annotation { "Feature Type Name" : "Feature", "Feature Type Description" : "" }
export const myFeature = defineFeature(function(context is Context, id is Id, definition is map)
    precondition{}
    {
        {
            assignVariable(context, id + "F0", {"name" : "T", "anyValue" : 0});
        }
        {
            var Q0;
            Q0=qCreatedBy(makeId("Front.planeOp"),FACE);
            var sketch = newSketch(context, id + "F1", { "sketchPlane" : qUnion([Q0])});
            skArc(sketch, "E0", {"start": v(71.88, 0.4) * mm, "mid": v(0, 71.88) * mm, "end": v(-71.88, 0.4) * mm});
            skLineSegment(sketch, "E1", {"start": v(0, 0) * mm, "end": v(35.94, 0) * mm, "construction": true});
            skLineSegment(sketch, "E2.bottom", {"start": v(35.94, 0.4) * mm, "end": v(71.88, 0.4) * mm});
            skLineSegment(sketch, "E2.top", {"start": v(35.94, -0.4) * mm, "end": v(71.88, -0.4) * mm});
            skLineSegment(sketch, "E2.left", {"start": v(35.94, 0.4) * mm, "end": v(35.94, -0.4) * mm});
            skLineSegment(sketch, "E3", {"start": v(0, 0) * mm, "end": v(-35.94, 0) * mm, "construction": true});
            skLineSegment(sketch, "E4.bottom", {"start": v(-0.4, 0) * mm, "end": v(0.4, 0) * mm});
            skLineSegment(sketch, "E4.left", {"start": v(-0.4, 0) * mm, "end": v(-0.4, -71.88) * mm});
            skLineSegment(sketch, "E4.right", {"start": v(0.4, 0) * mm, "end": v(0.4, -71.88) * mm});
            skLineSegment(sketch, "E5.bottom", {"start": v(-35.94, 0.4) * mm, "end": v(-71.88, 0.4) * mm});
            skLineSegment(sketch, "E5.top", {"start": v(-35.94, -0.4) * mm, "end": v(-71.88, -0.4) * mm});
            skLineSegment(sketch, "E5.left", {"start": v(-35.94, 0.4) * mm, "end": v(-35.94, -0.4) * mm});
            skArc(sketch, "E6.trimOffspring", {"start": v(0.4, -71.88) * mm, "mid": v(50.83, -50.83) * mm, "end": v(71.88, -0.4) * mm});
            skArc(sketch, "E7.trimOffspring", {"start": v(-71.88, -0.4) * mm, "mid": v(-50.83, -50.83) * mm, "end": v(-0.4, -71.88) * mm});
            skText(sketch, "E8", { "text": "Efficial Knotball\nYou not up?", "fontName": "OpenSans-Regular.ttf"});
            const initialGuessF1  = {"E8": [-0.05627, 0.03652, 1, 0, 0.00569]};
            skSetInitialGuess(sketch, initialGuessF1);
            skSolve(sketch);
        }
        {
            var Q0;
            Q0=makeQuery(id+"F1.imprint","IMPRINT",FACE,{"disambiguationData":[TD([[makeQuery(id+"F1.imprint","IMPRINT",EDGE,{"derivedFrom":sQuery(id+"F1.wireOp",EDGE,"E0")}),1.0]])]});
            extrude(context, id + "F2", {"entities" : qUnion([Q0]), "depth" : (4 * getVariable(context, 'T')) * mm, "offsetDistance" : 25.4 * mm, "hasSecondDirection" : true, "secondDirectionOppositeDirection" : true, "secondDirectionDepth" : (4 * getVariable(context, 'T')) * mm});
        }
        {
            var Q0;
            Q0=qCreatedBy(makeId("Top.planeOp"),FACE);
            var sketch = newSketch(context, id + "F3", { "sketchPlane" : qUnion([Q0])});
            skArc(sketch, "E9", {"start": v(0.4, -71.88) * mm, "mid": v(0, 71.88) * mm, "end": v(-0.4, -71.88) * mm});
            skLineSegment(sketch, "E10", {"start": v(0, 0) * mm, "end": v(35.94, 0) * mm, "construction": true});
            skLineSegment(sketch, "E11", {"start": v(0, 0) * mm, "end": v(-35.94, 0) * mm, "construction": true});
            skLineSegment(sketch, "E12.bottom", {"start": v(-0.4, 35.94) * mm, "end": v(0.4, 35.94) * mm});
            skLineSegment(sketch, "E12.left", {"start": v(-0.4, 35.94) * mm, "end": v(-0.4, 0.4) * mm});
            skLineSegment(sketch, "E12.right", {"start": v(0.4, 35.94) * mm, "end": v(0.4, 0.4) * mm});
            skLineSegment(sketch, "E13", {"start": v(0, 0) * mm, "end": v(0, 35.94) * mm, "construction": true});
            skLineSegment(sketch, "E14.bottom", {"start": v(-35.94, 0.4) * mm, "end": v(-0.4, 0.4) * mm});
            skLineSegment(sketch, "E14.top", {"start": v(-35.94, -0.4) * mm, "end": v(-0.4, -0.4) * mm});
            skLineSegment(sketch, "E14.left", {"start": v(-35.94, 0.4) * mm, "end": v(-35.94, -0.4) * mm});
            skLineSegment(sketch, "E14.right", {"start": v(35.94, 0.4) * mm, "end": v(35.94, -0.4) * mm});
            skLineSegment(sketch, "E15.trimOffspring", {"start": v(-0.4, -0.4) * mm, "end": v(-0.4, -71.88) * mm});
            skLineSegment(sketch, "E16.trimOffspring", {"start": v(0.4, 0.4) * mm, "end": v(35.94, 0.4) * mm});
            skLineSegment(sketch, "E17.trimOffspring", {"start": v(0.4, -0.4) * mm, "end": v(35.94, -0.4) * mm});
            skLineSegment(sketch, "E18.trimOffspring", {"start": v(0.4, -0.4) * mm, "end": v(0.4, -71.88) * mm});
            skSolve(sketch);
        }
        {
            var Q0;
            Q0=makeQuery(id+"F3.imprint","IMPRINT",FACE,{"disambiguationData":[TD([[makeQuery(id+"F3.imprint","IMPRINT",EDGE,{"derivedFrom":sQuery(id+"F3.wireOp",EDGE,"E9")}),1.0]])]});
            extrude(context, id + "F4", {"entities" : qUnion([Q0]), "depth" : (4 * getVariable(context, 'T')) * mm, "offsetDistance" : 25.4 * mm, "hasSecondDirection" : true, "secondDirectionOppositeDirection" : true, "secondDirectionDepth" : (4 * getVariable(context, 'T')) * mm});
        }
        {
            var Q0;
            Q0=qCreatedBy(makeId("Right.planeOp"),FACE);
            var sketch = newSketch(context, id + "F5", { "sketchPlane" : qUnion([Q0])});
            skArc(sketch, "E19", {"start": v(-0.4, 71.88) * mm, "mid": v(-50.83, -50.83) * mm, "end": v(71.88, -0.4) * mm});
            skLineSegment(sketch, "E20", {"start": v(0, 0) * mm, "end": v(0, 0) * mm});
            skLineSegment(sketch, "E21", {"start": v(0, 0) * mm, "end": v(35.94, 0) * mm, "construction": true});
            skLineSegment(sketch, "E22.bottom", {"start": v(-0.4, 0) * mm, "end": v(0.4, 0) * mm});
            skLineSegment(sketch, "E22.left", {"start": v(-0.4, 0) * mm, "end": v(-0.4, 71.88) * mm});
            skLineSegment(sketch, "E22.right", {"start": v(0.4, 0) * mm, "end": v(0.4, 71.88) * mm});
            skLineSegment(sketch, "E23.bottom", {"start": v(35.94, 0.4) * mm, "end": v(71.88, 0.4) * mm});
            skLineSegment(sketch, "E23.top", {"start": v(35.94, -0.4) * mm, "end": v(71.88, -0.4) * mm});
            skLineSegment(sketch, "E23.left", {"start": v(35.94, 0.4) * mm, "end": v(35.94, -0.4) * mm});
            skArc(sketch, "E24.trimOffspring", {"start": v(71.88, 0.4) * mm, "mid": v(50.83, 50.83) * mm, "end": v(0.4, 71.88) * mm});
            skSolve(sketch);
        }
        {
            var Q0;
            Q0=makeQuery(id+"F5.imprint","IMPRINT",FACE,{"disambiguationData":[TD([[makeQuery(id+"F5.imprint","IMPRINT",EDGE,{"derivedFrom":sQuery(id+"F5.wireOp",EDGE,"E19")}),1.0]])]});
            extrude(context, id + "F6", {"entities" : qUnion([Q0]), "depth" : (4 * getVariable(context, 'T')) * mm, "offsetDistance" : 25.4 * mm, "hasSecondDirection" : true, "secondDirectionOppositeDirection" : true, "secondDirectionDepth" : (4 * getVariable(context, 'T')) * mm});
        }
    });